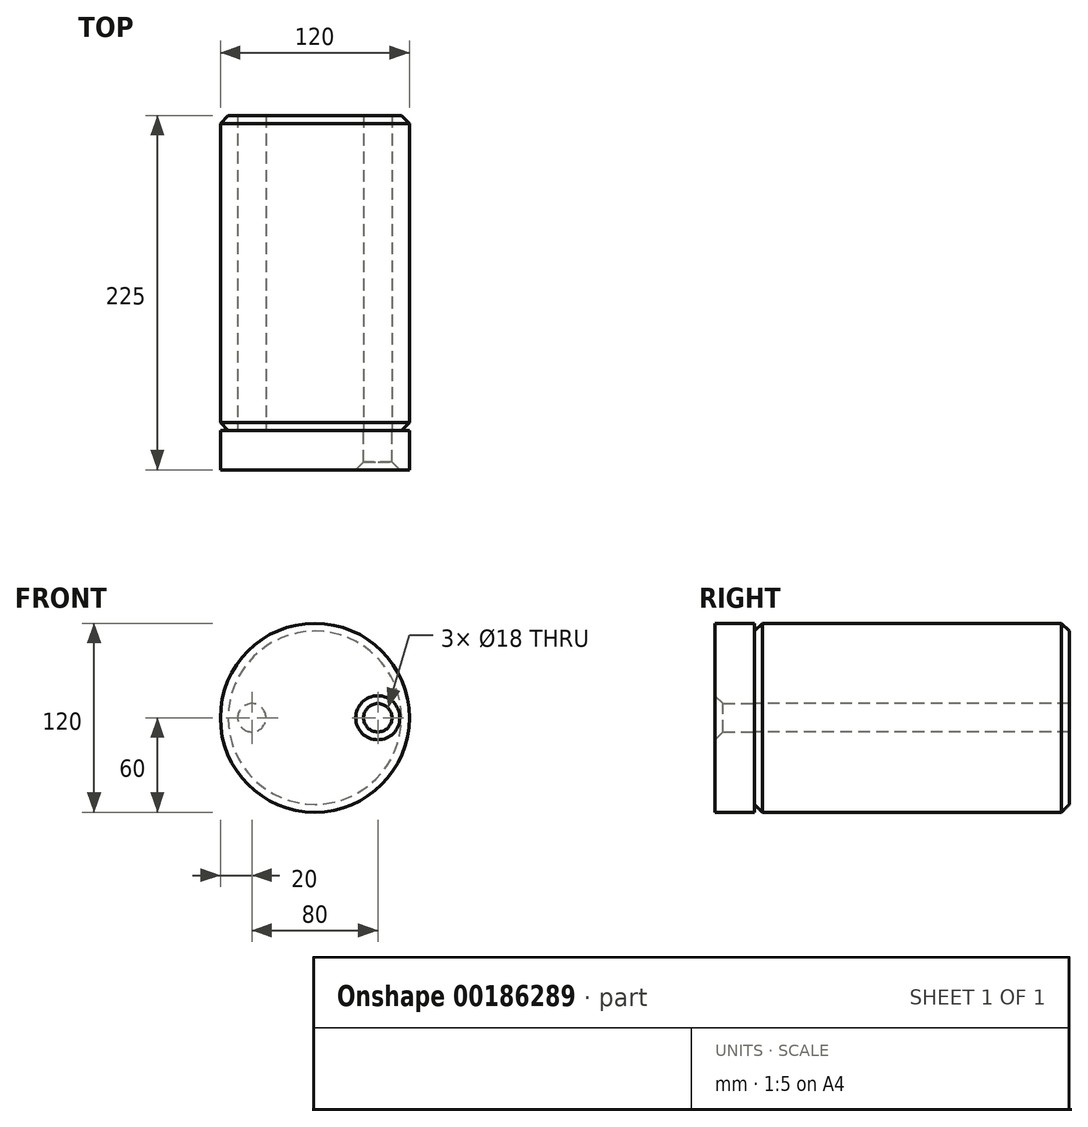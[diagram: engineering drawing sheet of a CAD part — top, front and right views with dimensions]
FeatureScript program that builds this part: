
annotation { "Feature Type Name" : "Feature", "Feature Type Description" : "" }
export const myFeature = defineFeature(function(context is Context, id is Id, definition is map)
    precondition{}
    {
        {
            var Q0;
            Q0=qCreatedBy(makeId("Front.planeOp"),FACE);
            var sketch = newSketch(context, id + "F0", { "sketchPlane" : qUnion([Q0])});
            skCircle(sketch, "E0", {"center": v(0, 0) * mm, "radius": 60 * mm});
            skLineSegment(sketch, "E1", {"start": v(-60, 0) * mm, "end": v(60, 0) * mm, "construction": true});
            skLineSegment(sketch, "E2", {"start": v(0, 60) * mm, "end": v(0, -60) * mm, "construction": true});
            skCircle(sketch, "E3", {"center": v(-40, 0) * mm, "radius": 9 * mm});
            skCircle(sketch, "E4.MirrorC", {"center": v(40, 0) * mm, "radius": 9 * mm});
            skSolve(sketch);
        }
        {
            var Q0;
            Q0=makeQuery(id+"F0.imprint","IMPRINT",FACE,{"disambiguationData":[TD([[makeQuery(id+"F0.imprint","IMPRINT",EDGE,{"derivedFrom":sQuery(id+"F0.wireOp",EDGE,"E3")}),1.0]])]});
            var Q1;
            Q1=makeQuery(id+"F0.imprint","IMPRINT",FACE,{"disambiguationData":[TD([[makeQuery(id+"F0.imprint","IMPRINT",EDGE,{"derivedFrom":sQuery(id+"F0.wireOp",EDGE,"E4.MirrorC")}),-1.0]])]});
            extrude(context, id + "F1", {"entities" : qUnion([Q0, Q1]), "depth" : 25 * mm});
        }
        {
            var Q0;
            Q0 = qSketchRegion(id + "F0", true);
            extrude(context, id + "F2", {"entities" : qUnion([Q0]), "oppositeDirection" : true, "depth" : 200 * mm});
        }
        {
            var Q0;
            Q0=makeQuery(id+"F2.opExtrude","CAP_EDGE",EDGE,{"disambiguationData":[OSD([sQuery(id+"F0.wireOp",EDGE,"E0")])],"isStart":false});
            var Q1;
            Q1=makeQuery(id+"F2.opExtrude","SWEPT_FACE",FACE,{"disambiguationData":[OSD([sQuery(id+"F0.wireOp",EDGE,"E0")])]});
            var Q2;
            Q2=makeQuery(id+"F1.opExtrude","CAP_EDGE",EDGE,{"disambiguationData":[OSD([sQuery(id+"F0.wireOp",EDGE,"E3")])],"isStart":false});
            chamfer(context, id + "F3", {"entities" : qUnion([Q0, Q1, Q2]), "width" : 5 * mm, "tangentPropagation" : true});
        }
        {
            var Q0;
            Q0=makeQuery(id+"F1.opExtrude","CAP_EDGE",EDGE,{"disambiguationData":[OSD([sQuery(id+"F0.wireOp",EDGE,"E4.MirrorC")])],"isStart":false});
            chamfer(context, id + "F4", {"entities" : qUnion([Q0]), "width" : 5 * mm, "tangentPropagation" : true});
        }
    });
